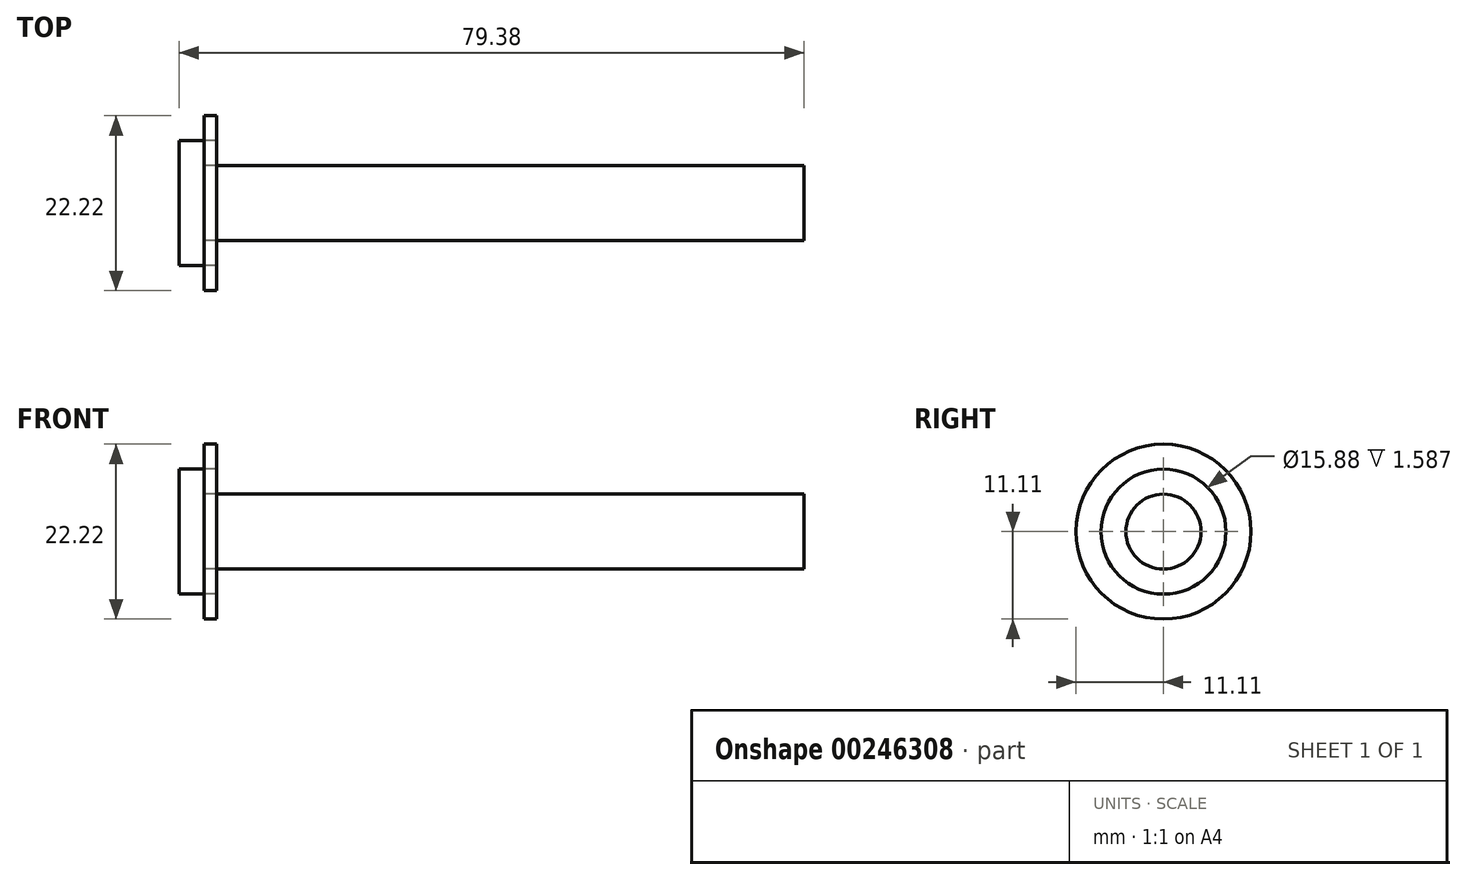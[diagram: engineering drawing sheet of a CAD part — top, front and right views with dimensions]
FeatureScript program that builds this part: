
annotation { "Feature Type Name" : "Feature", "Feature Type Description" : "" }
export const myFeature = defineFeature(function(context is Context, id is Id, definition is map)
    precondition{}
    {
        {
            var Q0;
            Q0=qCreatedBy(makeId("Right.planeOp"),FACE);
            var sketch = newSketch(context, id + "F0", { "sketchPlane" : qUnion([Q0])});
            skCircle(sketch, "E0", {"center": v(0, 0) * mm, "radius": 4.76 * mm});
            skSolve(sketch);
        }
        {
            var Q0;
            Q0=makeQuery(id+"F0.imprint","IMPRINT",FACE,{"disambiguationData":[TD([[makeQuery(id+"F0.imprint","IMPRINT",EDGE,{"derivedFrom":sQuery(id+"F0.wireOp",EDGE,"E0")}),1.0]])]});
            extrude(context, id + "F1", {"entities" : qUnion([Q0]), "depth" : 76.2 * mm});
        }
        {
            var Q0;
            Q0=qCreatedBy(makeId("Right.planeOp"),FACE);
            var sketch = newSketch(context, id + "F2", { "sketchPlane" : qUnion([Q0])});
            skCircle(sketch, "E1", {"center": v(0, 0) * mm, "radius": 7.94 * mm});
            skCircle(sketch, "E2", {"center": v(0, 0) * mm, "radius": 11.11 * mm});
            skSolve(sketch);
        }
        {
            var Q0;
            Q0=makeQuery(id+"F2.imprint","IMPRINT",FACE,{"disambiguationData":[TD([[makeQuery(id+"F2.imprint","IMPRINT",EDGE,{"derivedFrom":sQuery(id+"F2.wireOp",EDGE,"E1")}),-1.0]])]});
            extrude(context, id + "F3", {"entities" : qUnion([Q0]), "depth" : 1.59 * mm});
        }
        {
            var Q0;
            Q0=makeQuery(id+"F2.imprint","IMPRINT",FACE,{"disambiguationData":[TD([[makeQuery(id+"F2.imprint","IMPRINT",EDGE,{"derivedFrom":sQuery(id+"F2.wireOp",EDGE,"E1")}),1.0]])]});
            extrude(context, id + "F4", {"entities" : qUnion([Q0]), "oppositeDirection" : true, "depth" : 3.17 * mm});
        }
    });
